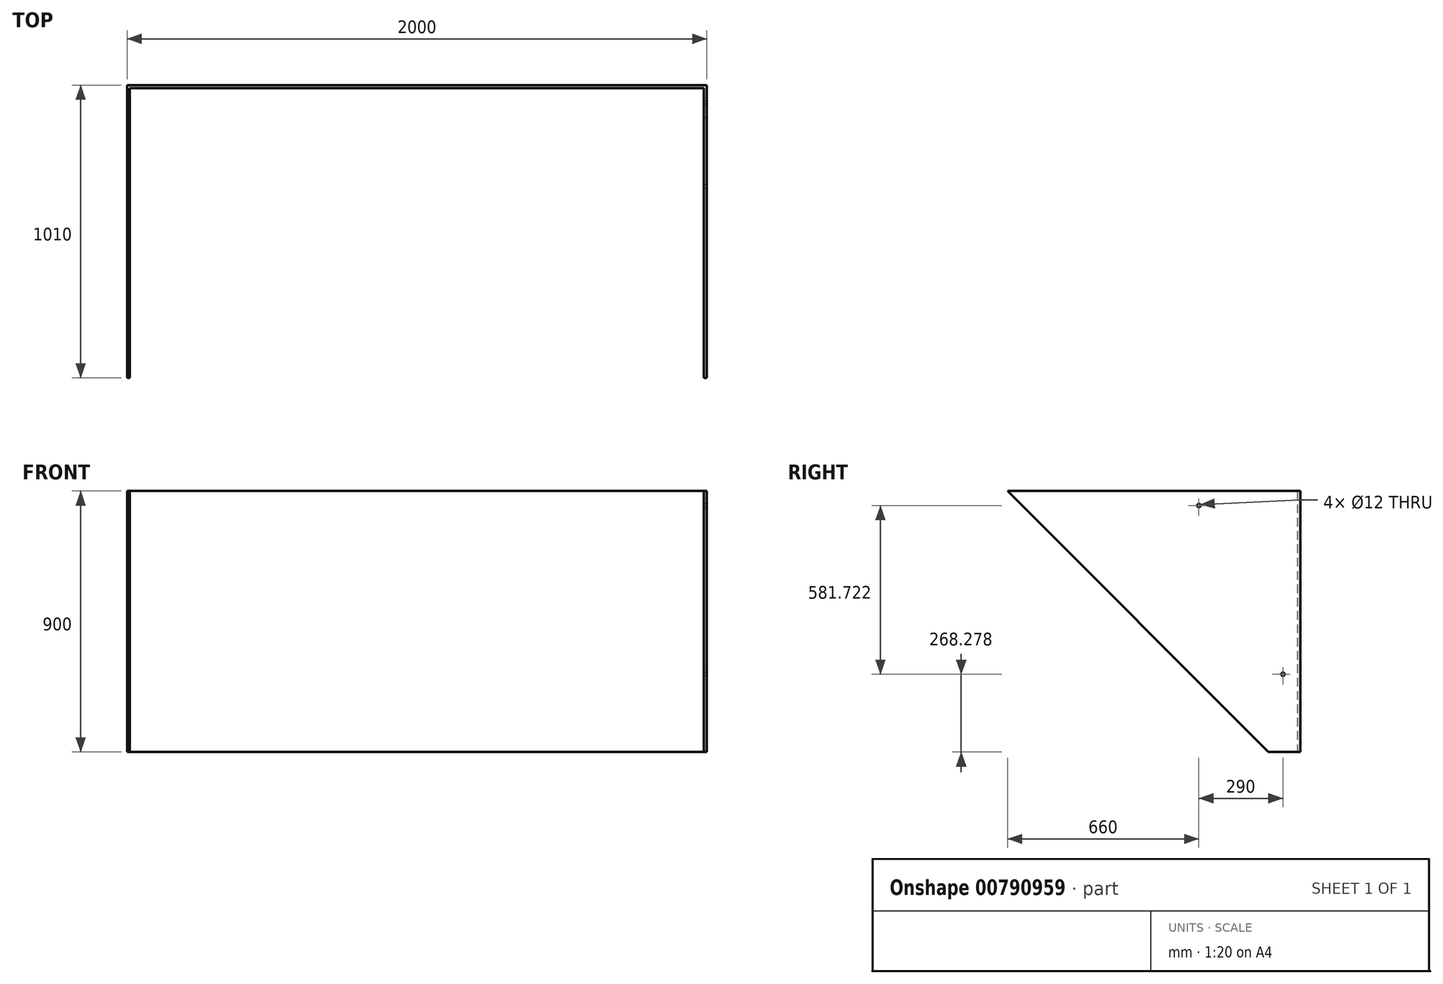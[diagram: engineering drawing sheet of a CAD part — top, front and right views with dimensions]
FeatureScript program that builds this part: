
annotation { "Feature Type Name" : "Feature", "Feature Type Description" : "" }
export const myFeature = defineFeature(function(context is Context, id is Id, definition is map)
    precondition{}
    {
        {
            var Q0;
            Q0=qCreatedBy(makeId("Front.planeOp"),FACE);
            var sketch = newSketch(context, id + "F0", { "sketchPlane" : qUnion([Q0])});
            skLineSegment(sketch, "E0.bottom", {"start": v(-1000, 450) * mm, "end": v(1000, 450) * mm});
            skLineSegment(sketch, "E0.top", {"start": v(-1000, -450) * mm, "end": v(1000, -450) * mm});
            skLineSegment(sketch, "E0.left", {"start": v(-1000, 450) * mm, "end": v(-1000, -450) * mm});
            skLineSegment(sketch, "E0.right", {"start": v(1000, 450) * mm, "end": v(1000, -450) * mm});
            skPoint(sketch, "E0.middle", {"position": v(0, 0) * mm});
            skSolve(sketch);
        }
        {
            var Q0;
            Q0=makeQuery(id+"F0.imprint","IMPRINT",FACE,{"disambiguationData":[TD([[makeQuery(id+"F0.imprint","IMPRINT",EDGE,{"derivedFrom":sQuery(id+"F0.wireOp",EDGE,"E0.bottom")}),-1.0]])]});
            extrude(context, id + "F1", {"entities" : qUnion([Q0]), "endBound" : BoundingType.SYMMETRIC, "depth" : 10 * mm, "offsetDistance" : 25 * mm});
        }
        {
            var Q0;
            Q0=makeQuery(id+"F1.opExtrude","CAP_FACE",FACE,{"disambiguationData":[OSD([sQuery(id+"F0.wireOp",EDGE,"E0.bottom"),sQuery(id+"F0.wireOp",EDGE,"E0.top"),sQuery(id+"F0.wireOp",EDGE,"E0.left"),sQuery(id+"F0.wireOp",EDGE,"E0.right")])],"isStart":false});
            var sketch = newSketch(context, id + "F2", { "sketchPlane" : qUnion([Q0])});
            skLineSegment(sketch, "E1.bottom", {"start": v(1000, 450) * mm, "end": v(990, 450) * mm});
            skLineSegment(sketch, "E1.top", {"start": v(1000, -450) * mm, "end": v(990, -450) * mm});
            skLineSegment(sketch, "E1.left", {"start": v(1000, 450) * mm, "end": v(1000, -450) * mm});
            skLineSegment(sketch, "E1.right", {"start": v(990, 450) * mm, "end": v(990, -450) * mm});
            skLineSegment(sketch, "E2.bottom", {"start": v(-1000, 450) * mm, "end": v(-990, 450) * mm});
            skLineSegment(sketch, "E2.top", {"start": v(-1000, -450) * mm, "end": v(-990, -450) * mm});
            skLineSegment(sketch, "E2.left", {"start": v(-1000, 450) * mm, "end": v(-1000, -450) * mm});
            skLineSegment(sketch, "E2.right", {"start": v(-990, 450) * mm, "end": v(-990, -450) * mm});
            skSolve(sketch);
        }
        {
            var Q0;
            Q0=makeQuery(id+"F2.imprint","IMPRINT",FACE,{"disambiguationData":[TD([[makeQuery(id+"F2.imprint","IMPRINT",EDGE,{"derivedFrom":sQuery(id+"F2.wireOp",EDGE,"E2.bottom")}),-1.0]])]});
            var Q1;
            Q1=makeQuery(id+"F2.imprint","IMPRINT",FACE,{"disambiguationData":[TD([[makeQuery(id+"F2.imprint","IMPRINT",EDGE,{"derivedFrom":sQuery(id+"F2.wireOp",EDGE,"E1.bottom")}),-1.0]])]});
            extrude(context, id + "F3", {"entities" : qUnion([Q0, Q1]), "operationType" : NewBodyOperationType.ADD, "depth" : 1000 * mm, "offsetDistance" : 25 * mm});
        }
        {
            var Q0;
            Q0=makeQuery(id+"F3.boolean.opBoolean","MERGE",FACE,{"derivedFrom":[makeQuery(id+"F1.opExtrude","SWEPT_FACE",FACE,{"disambiguationData":[OSD([sQuery(id+"F0.wireOp",EDGE,"E0.right")])]}),makeQuery(id+"F3.opExtrude","SWEPT_FACE",FACE,{"disambiguationData":[OSD([sQuery(id+"F2.wireOp",EDGE,"E1.left")])]})]});
            var sketch = newSketch(context, id + "F4", { "sketchPlane" : qUnion([Q0])});
            skLineSegment(sketch, "E3", {"start": v(-1005, 450) * mm, "end": v(-1005, -450) * mm});
            skLineSegment(sketch, "E4", {"start": v(-1005, -450) * mm, "end": v(-105, -450) * mm});
            skLineSegment(sketch, "E5", {"start": v(-105, -450) * mm, "end": v(-1005, 450) * mm});
            skSolve(sketch);
        }
        {
            var Q0;
            Q0=makeQuery(id+"F4.imprint","IMPRINT",FACE,{"disambiguationData":[TD([[makeQuery(id+"F4.imprint","IMPRINT",EDGE,{"derivedFrom":sQuery(id+"F4.wireOp",EDGE,"E3")}),1.0]])]});
            extrude(context, id + "F5", {"entities" : qUnion([Q0]), "operationType" : NewBodyOperationType.REMOVE, "endBound" : BoundingType.THROUGH_ALL, "oppositeDirection" : true, "depth" : 25 * mm});
        }
        {
            var Q0;
            Q0=makeQuery(id+"F3.boolean.opBoolean","MERGE",FACE,{"derivedFrom":[makeQuery(id+"F1.opExtrude","SWEPT_FACE",FACE,{"disambiguationData":[OSD([sQuery(id+"F0.wireOp",EDGE,"E0.left")])]}),makeQuery(id+"F3.opExtrude","SWEPT_FACE",FACE,{"disambiguationData":[OSD([sQuery(id+"F2.wireOp",EDGE,"E2.left")])]})]});
            var sketch = newSketch(context, id + "F6", { "sketchPlane" : qUnion([Q0])});
            skLineSegment(sketch, "E6", {"start": v(-5, 450) * mm, "end": v(345, 450) * mm});
            skLineSegment(sketch, "E7", {"start": v(345, 450) * mm, "end": v(345, 400) * mm});
            skPoint(sketch, "E8", {"position": v(345, 400) * mm});
            skLineSegment(sketch, "E9", {"start": v(-5, -450) * mm, "end": v(55, -450) * mm, "construction": true});
            skLineSegment(sketch, "E10", {"start": v(55, -450) * mm, "end": v(55, 450) * mm, "construction": true});
            skLineSegment(sketch, "E11", {"start": v(345, 400) * mm, "end": v(55, -181.72) * mm});
            skPoint(sketch, "E12", {"position": v(55, -181.72) * mm});
            skSolve(sketch);
        }
        {
            var Q0;
            Q0=sQuery(id+"F6.wireOp",VERTEX,"E8");
            var Q1;
            Q1=sQuery(id+"F6.wireOp",VERTEX,"E12");
            var Q2;
            Q2=makeQuery(id+"F1.opExtrude","SWEPT_BODY",BODY,{"disambiguationData":[OSD([sQuery(id+"F0.wireOp",EDGE,"E0.bottom"),sQuery(id+"F0.wireOp",EDGE,"E0.top"),sQuery(id+"F0.wireOp",EDGE,"E0.left"),sQuery(id+"F0.wireOp",EDGE,"E0.right")])]});
            hole(context, id + "F7", {"style" : HoleStyle.SIMPLE, "endStyle" : HoleEndStyle.THROUGH, "holeDiameter" : 12 * mm, "isTappedThrough" : true, "tappedDepth" : 12 * mm, "tapClearance" : 3, "locations" : qUnion([Q0, Q1]), "scope" : qUnion([Q2])});
        }
    });
